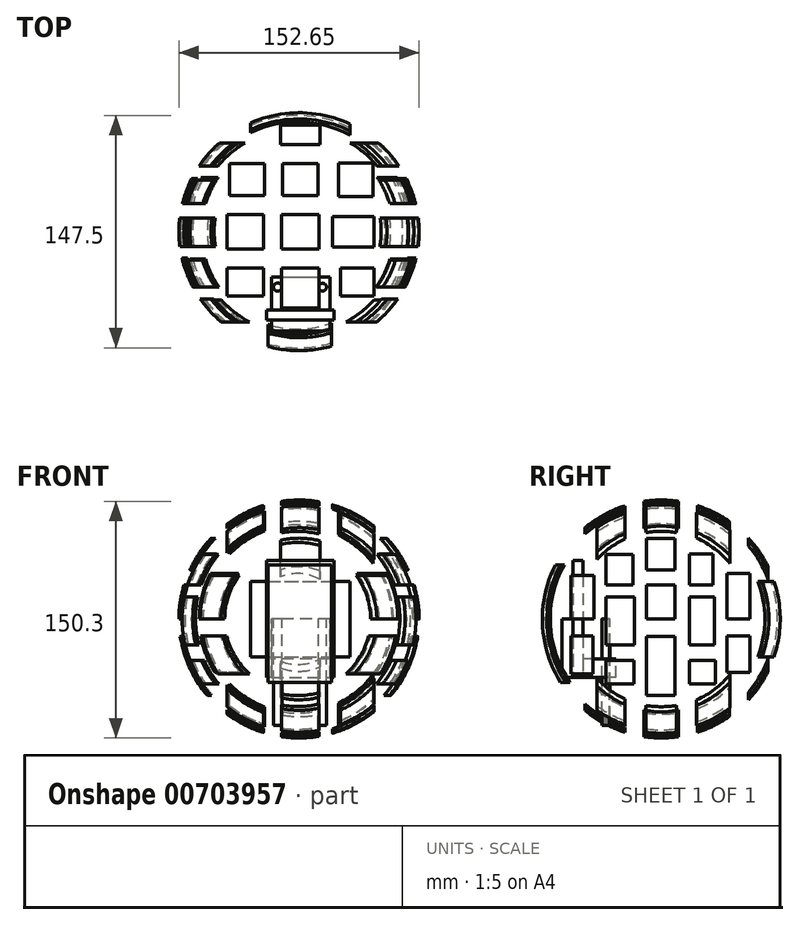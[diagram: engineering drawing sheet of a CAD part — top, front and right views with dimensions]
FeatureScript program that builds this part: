
annotation { "Feature Type Name" : "Feature", "Feature Type Description" : "" }
export const myFeature = defineFeature(function(context is Context, id is Id, definition is map)
    precondition{}
    {
        {
            var Q0;
            Q0=qCreatedBy(makeId("Front.planeOp"),FACE);
            var sketch = newSketch(context, id + "F0", { "sketchPlane" : qUnion([Q0])});
            skArc(sketch, "E0", {"start": v(75.5, 0) * mm, "mid": v(-0.83, 75.54) * mm, "end": v(-77.15, 0) * mm});
            skLineSegment(sketch, "E1", {"start": v(-77.15, 0) * mm, "end": v(75.5, 0) * mm});
            skLineSegment(sketch, "E2", {"start": v(-77.15, 0) * mm, "end": v(-98.73, 0) * mm});
            skLineSegment(sketch, "E3", {"start": v(-98.73, 0) * mm, "end": v(93.51, 0) * mm});
            skSolve(sketch);
        }
        {
            var Q0;
            Q0 = qSketchRegion(id + "F0", true);
            var Q1;
            Q1=sQuery(id+"F0.wireOp",EDGE,"E3");
            revolve(context, id + "F1", {"surfaceOperationType" : NewSurfaceOperationType.NEW, "entities" : qUnion([Q0]), "axis" : qUnion([Q1]), "revolveType" : RevolveType.FULL});
        }
        {
            var Q0;
            Q0=qCreatedBy(makeId("Top.planeOp"),FACE);
            var sketch = newSketch(context, id + "F2", { "sketchPlane" : qUnion([Q0])});
            skLineSegment(sketch, "E4.bottom", {"start": v(11.8, 10.88) * mm, "end": v(-11.8, 10.88) * mm});
            skLineSegment(sketch, "E4.top", {"start": v(11.8, -10.88) * mm, "end": v(-11.8, -10.88) * mm});
            skLineSegment(sketch, "E4.left", {"start": v(11.8, 10.88) * mm, "end": v(11.8, -10.88) * mm});
            skLineSegment(sketch, "E4.right", {"start": v(-11.8, 10.88) * mm, "end": v(-11.8, -10.88) * mm});
            skPoint(sketch, "E4.middle", {"position": v(0, 0) * mm});
            skLineSegment(sketch, "E5.bottom", {"start": v(11.8, -23.05) * mm, "end": v(-11.8, -23.05) * mm});
            skLineSegment(sketch, "E5.top", {"start": v(11.8, -48.4) * mm, "end": v(-11.8, -48.4) * mm});
            skLineSegment(sketch, "E5.left", {"start": v(11.8, -23.05) * mm, "end": v(11.8, -48.4) * mm});
            skLineSegment(sketch, "E5.right", {"start": v(-11.8, -23.05) * mm, "end": v(-11.8, -48.4) * mm});
            skPoint(sketch, "E5.middle", {"position": v(0, -35.72) * mm});
            skPoint(sketch, "E5.middle.positionSnap0", {"position": v(0, -10.88) * mm});
            skPoint(sketch, "E5.centerSnap0", {"position": v(0, -10.88) * mm});
            skLineSegment(sketch, "E6.bottom", {"start": v(11.4, 43.22) * mm, "end": v(-11.4, 43.22) * mm});
            skLineSegment(sketch, "E6.top", {"start": v(11.4, 22.83) * mm, "end": v(-11.4, 22.83) * mm});
            skLineSegment(sketch, "E6.left", {"start": v(11.4, 43.22) * mm, "end": v(11.4, 22.83) * mm});
            skLineSegment(sketch, "E6.right", {"start": v(-11.4, 43.22) * mm, "end": v(-11.4, 22.83) * mm});
            skPoint(sketch, "E6.middle", {"position": v(0, 33.03) * mm});
            skLineSegment(sketch, "E7.bottom", {"start": v(-23.48, 10.88) * mm, "end": v(-46.43, 10.88) * mm});
            skLineSegment(sketch, "E7.top", {"start": v(-23.48, -10.88) * mm, "end": v(-46.43, -10.88) * mm});
            skLineSegment(sketch, "E7.left", {"start": v(-23.48, 10.88) * mm, "end": v(-23.48, -10.88) * mm});
            skLineSegment(sketch, "E7.right", {"start": v(-46.43, 10.88) * mm, "end": v(-46.43, -10.88) * mm});
            skPoint(sketch, "E7.middle", {"position": v(-34.96, 0) * mm});
            skLineSegment(sketch, "E8.bottom", {"start": v(46.66, 9.6) * mm, "end": v(20.3, 9.6) * mm});
            skLineSegment(sketch, "E8.top", {"start": v(46.66, -9.6) * mm, "end": v(20.3, -9.6) * mm});
            skLineSegment(sketch, "E8.left", {"start": v(46.66, 9.6) * mm, "end": v(46.66, -9.6) * mm});
            skLineSegment(sketch, "E8.right", {"start": v(20.3, 9.6) * mm, "end": v(20.3, -9.6) * mm});
            skPoint(sketch, "E8.middle", {"position": v(33.48, 0) * mm});
            skLineSegment(sketch, "E9.bottom", {"start": v(46.24, 43.65) * mm, "end": v(24.12, 43.65) * mm});
            skLineSegment(sketch, "E9.top", {"start": v(46.24, 22.4) * mm, "end": v(24.12, 22.4) * mm});
            skLineSegment(sketch, "E9.left", {"start": v(46.24, 43.65) * mm, "end": v(46.24, 22.4) * mm});
            skLineSegment(sketch, "E9.right", {"start": v(24.12, 43.65) * mm, "end": v(24.12, 22.4) * mm});
            skPoint(sketch, "E9.middle", {"position": v(35.18, 33.03) * mm});
            skLineSegment(sketch, "E10.bottom", {"start": v(-22.6, 43.22) * mm, "end": v(-44.88, 43.22) * mm});
            skLineSegment(sketch, "E10.top", {"start": v(-22.6, 22.83) * mm, "end": v(-44.88, 22.83) * mm});
            skLineSegment(sketch, "E10.left", {"start": v(-22.6, 43.22) * mm, "end": v(-22.6, 22.83) * mm});
            skLineSegment(sketch, "E10.right", {"start": v(-44.88, 43.22) * mm, "end": v(-44.88, 22.83) * mm});
            skPoint(sketch, "E10.middle", {"position": v(-33.74, 33.03) * mm});
            skLineSegment(sketch, "E11.bottom", {"start": v(12.66, 67.86) * mm, "end": v(-12.66, 67.86) * mm});
            skLineSegment(sketch, "E11.top", {"start": v(12.66, 55.43) * mm, "end": v(-12.66, 55.43) * mm});
            skLineSegment(sketch, "E11.left", {"start": v(12.66, 67.86) * mm, "end": v(12.66, 55.43) * mm});
            skLineSegment(sketch, "E11.right", {"start": v(-12.66, 67.86) * mm, "end": v(-12.66, 55.43) * mm});
            skPoint(sketch, "E11.middle", {"position": v(0, 61.65) * mm});
            skLineSegment(sketch, "E12.bottom", {"start": v(46.66, -23.05) * mm, "end": v(25.46, -23.05) * mm});
            skLineSegment(sketch, "E12.top", {"start": v(46.66, -40.9) * mm, "end": v(25.46, -40.9) * mm});
            skLineSegment(sketch, "E12.left", {"start": v(46.66, -23.05) * mm, "end": v(46.66, -40.9) * mm});
            skLineSegment(sketch, "E12.right", {"start": v(25.46, -23.05) * mm, "end": v(25.46, -40.9) * mm});
            skPoint(sketch, "E12.middle", {"position": v(36.06, -31.98) * mm});
            skLineSegment(sketch, "E13.bottom", {"start": v(-23.48, -23.05) * mm, "end": v(-46.43, -23.05) * mm});
            skLineSegment(sketch, "E13.top", {"start": v(-23.48, -40.9) * mm, "end": v(-46.43, -40.9) * mm});
            skLineSegment(sketch, "E13.left", {"start": v(-23.48, -23.05) * mm, "end": v(-23.48, -40.9) * mm});
            skLineSegment(sketch, "E13.right", {"start": v(-46.43, -23.05) * mm, "end": v(-46.43, -40.9) * mm});
            skPoint(sketch, "E13.middle", {"position": v(-34.96, -31.98) * mm});
            skPoint(sketch, "E13.cornerSnap0", {"position": v(-23.48, 0) * mm});
            skSolve(sketch);
        }
        {
            var Q0;
            Q0 = qSketchRegion(id + "F2", true);
            extrude(context, id + "F3", {"entities" : qUnion([Q0]), "operationType" : NewBodyOperationType.REMOVE, "endBound" : BoundingType.SYMMETRIC, "depth" : 301.9 * mm, "offsetDistance" : 25.4 * mm});
        }
        {
            var Q0;
            Q0=qCreatedBy(makeId("Front.planeOp"),FACE);
            var sketch = newSketch(context, id + "F4", { "sketchPlane" : qUnion([Q0])});
            skLineSegment(sketch, "E14", {"start": v(-75.42, 0) * mm, "end": v(72.08, 0) * mm});
            skArc(sketch, "E15", {"start": v(72.08, 0) * mm, "mid": v(-1.67, 73.75) * mm, "end": v(-75.42, 0) * mm});
            skSolve(sketch);
        }
        {
            var Q0;
            Q0 = qSketchRegion(id + "F4", true);
            var Q1;
            Q1=sQuery(id+"F4.wireOp",EDGE,"E14");
            revolve(context, id + "F5", {"operationType" : NewBodyOperationType.REMOVE, "surfaceOperationType" : NewSurfaceOperationType.NEW, "entities" : qUnion([Q0]), "axis" : qUnion([Q1]), "revolveType" : RevolveType.FULL, "oppositeDirection" : true});
        }
        {
            var Q0;
            Q0=qCreatedBy(makeId("Front.planeOp"),FACE);
            var sketch = newSketch(context, id + "F6", { "sketchPlane" : qUnion([Q0])});
            skLineSegment(sketch, "E16.bottom", {"start": v(-20.54, 34.32) * mm, "end": v(19.94, 34.32) * mm});
            skLineSegment(sketch, "E16.top", {"start": v(-20.54, -40.2) * mm, "end": v(19.94, -40.2) * mm});
            skLineSegment(sketch, "E16.left", {"start": v(-20.54, 34.32) * mm, "end": v(-20.54, -40.2) * mm});
            skLineSegment(sketch, "E16.right", {"start": v(19.94, 34.32) * mm, "end": v(19.94, -40.2) * mm});
            skSolve(sketch);
        }
        {
            var Q0;
            Q0 = qSketchRegion(id + "F6", true);
            extrude(context, id + "F7", {"entities" : qUnion([Q0]), "operationType" : NewBodyOperationType.REMOVE, "depth" : 174.95 * mm, "offsetDistance" : 25.4 * mm});
        }
        {
            var Q0;
            Q0=qCreatedBy(makeId("Right.planeOp"),FACE);
            var sketch = newSketch(context, id + "F8", { "sketchPlane" : qUnion([Q0])});
            skLineSegment(sketch, "E17.bottom", {"start": v(-9.27, 51.22) * mm, "end": v(8.56, 51.22) * mm});
            skLineSegment(sketch, "E17.top", {"start": v(-9.27, 31.3) * mm, "end": v(8.56, 31.3) * mm});
            skLineSegment(sketch, "E17.left", {"start": v(-9.27, 51.22) * mm, "end": v(-9.27, 31.3) * mm});
            skLineSegment(sketch, "E17.right", {"start": v(8.56, 51.22) * mm, "end": v(8.56, 31.3) * mm});
            skLineSegment(sketch, "E18.bottom", {"start": v(-18.03, 40.92) * mm, "end": v(-35.01, 40.92) * mm});
            skLineSegment(sketch, "E18.top", {"start": v(-18.03, 21.6) * mm, "end": v(-35.01, 21.6) * mm});
            skLineSegment(sketch, "E18.left", {"start": v(-18.03, 40.92) * mm, "end": v(-18.03, 21.6) * mm});
            skLineSegment(sketch, "E18.right", {"start": v(-35.01, 40.92) * mm, "end": v(-35.01, 21.6) * mm});
            skLineSegment(sketch, "E19.bottom", {"start": v(-57.38, 27.8) * mm, "end": v(-42.72, 27.8) * mm});
            skLineSegment(sketch, "E19.top", {"start": v(-57.38, 0) * mm, "end": v(-42.72, 0) * mm});
            skLineSegment(sketch, "E19.left", {"start": v(-57.38, 27.8) * mm, "end": v(-57.38, 0) * mm});
            skLineSegment(sketch, "E19.right", {"start": v(-42.72, 27.8) * mm, "end": v(-42.72, 0) * mm});
            skLineSegment(sketch, "E20.bottom", {"start": v(-57.38, -10.76) * mm, "end": v(-43.5, -10.76) * mm});
            skLineSegment(sketch, "E20.top", {"start": v(-57.38, -34.79) * mm, "end": v(-43.5, -34.79) * mm});
            skLineSegment(sketch, "E20.left", {"start": v(-57.38, -10.76) * mm, "end": v(-57.38, -34.79) * mm});
            skLineSegment(sketch, "E20.right", {"start": v(-43.5, -10.76) * mm, "end": v(-43.5, -34.79) * mm});
            skPoint(sketch, "E21.firstSnap0", {"position": v(-42.72, 13.9) * mm});
            skLineSegment(sketch, "E21.bottom", {"start": v(-35.01, 13.9) * mm, "end": v(-16.88, 13.9) * mm});
            skLineSegment(sketch, "E21.top", {"start": v(-35.01, -16.55) * mm, "end": v(-16.88, -16.55) * mm});
            skLineSegment(sketch, "E21.left", {"start": v(-35.01, 13.9) * mm, "end": v(-35.01, -16.55) * mm});
            skLineSegment(sketch, "E21.right", {"start": v(-16.88, 13.9) * mm, "end": v(-16.88, -16.55) * mm});
            skLineSegment(sketch, "E22.bottom", {"start": v(-35.01, -26.38) * mm, "end": v(-17.27, -26.38) * mm});
            skLineSegment(sketch, "E22.top", {"start": v(-35.01, -41.29) * mm, "end": v(-17.27, -41.29) * mm});
            skLineSegment(sketch, "E22.left", {"start": v(-35.01, -26.38) * mm, "end": v(-35.01, -41.29) * mm});
            skLineSegment(sketch, "E22.right", {"start": v(-17.27, -26.38) * mm, "end": v(-17.27, -41.29) * mm});
            skLineSegment(sketch, "E23.bottom", {"start": v(-9.27, 21.6) * mm, "end": v(8.56, 21.6) * mm});
            skLineSegment(sketch, "E23.top", {"start": v(-9.27, 0) * mm, "end": v(8.56, 0) * mm});
            skLineSegment(sketch, "E23.left", {"start": v(-9.27, 21.6) * mm, "end": v(-9.27, 0) * mm});
            skLineSegment(sketch, "E23.right", {"start": v(8.56, 21.6) * mm, "end": v(8.56, 0) * mm});
            skLineSegment(sketch, "E24.bottom", {"start": v(-9.27, -11) * mm, "end": v(8.56, -11) * mm});
            skLineSegment(sketch, "E24.top", {"start": v(-9.27, -48.56) * mm, "end": v(8.56, -48.56) * mm});
            skLineSegment(sketch, "E24.left", {"start": v(-9.27, -11) * mm, "end": v(-9.27, -48.56) * mm});
            skLineSegment(sketch, "E24.right", {"start": v(8.56, -11) * mm, "end": v(8.56, -48.56) * mm});
            skPoint(sketch, "E25.firstSnap0", {"position": v(8.56, 41.26) * mm});
            skLineSegment(sketch, "E25.bottom", {"start": v(17.78, 41.26) * mm, "end": v(32.9, 41.26) * mm});
            skLineSegment(sketch, "E25.top", {"start": v(17.78, 21.63) * mm, "end": v(32.9, 21.63) * mm});
            skLineSegment(sketch, "E25.left", {"start": v(17.78, 41.26) * mm, "end": v(17.78, 21.63) * mm});
            skLineSegment(sketch, "E25.right", {"start": v(32.9, 41.26) * mm, "end": v(32.9, 21.63) * mm});
            skLineSegment(sketch, "E26.bottom", {"start": v(17.78, 13.9) * mm, "end": v(33.65, 13.9) * mm});
            skLineSegment(sketch, "E26.top", {"start": v(17.78, -16.55) * mm, "end": v(33.65, -16.55) * mm});
            skLineSegment(sketch, "E26.left", {"start": v(17.78, 13.9) * mm, "end": v(17.78, -16.55) * mm});
            skLineSegment(sketch, "E26.right", {"start": v(33.65, 13.9) * mm, "end": v(33.65, -16.55) * mm});
            skLineSegment(sketch, "E27.bottom", {"start": v(17.78, -26.38) * mm, "end": v(34.44, -26.38) * mm});
            skLineSegment(sketch, "E27.top", {"start": v(17.78, -41.23) * mm, "end": v(34.44, -41.23) * mm});
            skLineSegment(sketch, "E27.left", {"start": v(17.78, -26.38) * mm, "end": v(17.78, -41.23) * mm});
            skLineSegment(sketch, "E27.right", {"start": v(34.44, -26.38) * mm, "end": v(34.44, -41.23) * mm});
            skLineSegment(sketch, "E28.bottom", {"start": v(41.8, 28.96) * mm, "end": v(56.43, 28.96) * mm});
            skLineSegment(sketch, "E28.top", {"start": v(41.8, 0) * mm, "end": v(56.43, 0) * mm});
            skLineSegment(sketch, "E28.left", {"start": v(41.8, 28.96) * mm, "end": v(41.8, 0) * mm});
            skLineSegment(sketch, "E28.right", {"start": v(56.43, 28.96) * mm, "end": v(56.43, 0) * mm});
            skPoint(sketch, "E29.oppositeSnap0", {"position": v(34.44, -33.8) * mm});
            skLineSegment(sketch, "E29.bottom", {"start": v(41.8, -10.76) * mm, "end": v(56.42, -10.76) * mm});
            skLineSegment(sketch, "E29.top", {"start": v(41.8, -33.8) * mm, "end": v(56.42, -33.8) * mm});
            skLineSegment(sketch, "E29.left", {"start": v(41.8, -10.76) * mm, "end": v(41.8, -33.8) * mm});
            skLineSegment(sketch, "E29.right", {"start": v(56.42, -10.76) * mm, "end": v(56.42, -33.8) * mm});
            skSolve(sketch);
        }
        {
            var Q0;
            Q0 = qSketchRegion(id + "F8", true);
            extrude(context, id + "F9", {"entities" : qUnion([Q0]), "operationType" : NewBodyOperationType.REMOVE, "endBound" : BoundingType.SYMMETRIC, "depth" : 251.44 * mm, "offsetDistance" : 25.4 * mm});
        }
        {
            var Q0;
            Q0=qCreatedBy(makeId("Front.planeOp"),FACE);
            var sketch = newSketch(context, id + "F10", { "sketchPlane" : qUnion([Q0])});
            skLineSegment(sketch, "E30.bottom", {"start": v(-31.6, 24) * mm, "end": v(31.6, 24) * mm});
            skLineSegment(sketch, "E30.top", {"start": v(-31.6, -24) * mm, "end": v(31.6, -24) * mm});
            skLineSegment(sketch, "E30.left", {"start": v(-31.6, 24) * mm, "end": v(-31.6, -24) * mm});
            skLineSegment(sketch, "E30.right", {"start": v(31.6, 24) * mm, "end": v(31.6, -24) * mm});
            skPoint(sketch, "E30.middle", {"position": v(0, 0) * mm});
            skSolve(sketch);
        }
        {
            var Q0;
            Q0 = qSketchRegion(id + "F10", true);
            extrude(context, id + "F11", {"entities" : qUnion([Q0]), "operationType" : NewBodyOperationType.REMOVE, "oppositeDirection" : true, "depth" : 141.65 * mm, "offsetDistance" : 25.4 * mm});
        }
        {
            var Q0;
            Q0=qCreatedBy(makeId("Top.planeOp"),FACE);
            var sketch = newSketch(context, id + "F12", { "sketchPlane" : qUnion([Q0])});
            skLineSegment(sketch, "E31.bottom", {"start": v(21.44, -49.8) * mm, "end": v(-21.44, -49.8) * mm});
            skLineSegment(sketch, "E31.top", {"start": v(21.44, -56) * mm, "end": v(-21.44, -56) * mm});
            skLineSegment(sketch, "E31.left", {"start": v(21.44, -49.8) * mm, "end": v(21.44, -56) * mm});
            skLineSegment(sketch, "E31.right", {"start": v(-21.44, -49.8) * mm, "end": v(-21.44, -56) * mm});
            skPoint(sketch, "E31.middle", {"position": v(0, -52.9) * mm});
            skSolve(sketch);
        }
        {
            var Q0;
            Q0 = qSketchRegion(id + "F12", true);
            extrude(context, id + "F13", {"entities" : qUnion([Q0]), "endBound" : BoundingType.SYMMETRIC, "depth" : 74.4 * mm, "offsetDistance" : 25.4 * mm});
        }
        {
            var Q0;
            Q0=qCreatedBy(makeId("Top.planeOp"),FACE);
            var sketch = newSketch(context, id + "F14", { "sketchPlane" : qUnion([Q0])});
            skLineSegment(sketch, "E32.bottom", {"start": v(-18.28, -28.73) * mm, "end": v(18.8, -28.73) * mm});
            skLineSegment(sketch, "E32.top", {"start": v(-18.28, -62.98) * mm, "end": v(18.8, -62.98) * mm});
            skLineSegment(sketch, "E32.left", {"start": v(-18.28, -28.73) * mm, "end": v(-18.28, -62.98) * mm});
            skLineSegment(sketch, "E32.right", {"start": v(18.8, -28.73) * mm, "end": v(18.8, -62.98) * mm});
            skSolve(sketch);
        }
        {
            var Q0;
            Q0=makeQuery(id+"F14.imprint","IMPRINT",FACE,{"disambiguationData":[TD([[makeQuery(id+"F14.imprint","IMPRINT",EDGE,{"derivedFrom":sQuery(id+"F14.wireOp",EDGE,"E32.bottom")}),-1.0]])]});
            var Q1;
            Q1=sQuery(id+"F14.wireOp",EDGE,"E32.bottom");
            extrude(context, id + "F15", {"entities" : qUnion([Q0]), "operationType" : NewBodyOperationType.ADD, "surfaceEntities" : qUnion([Q1]), "oppositeDirection" : true, "depth" : 37.2 * mm, "offsetDistance" : 25.4 * mm});
        }
        {
            var Q0;
            {var subQ0=sQuery(id+"F14.wireOp",EDGE,"E32.bottom");var subQ1=sQuery(id+"F14.wireOp",EDGE,"E32.right");var subQ2=sQuery(id+"F14.wireOp",EDGE,"E32.left");Q0=makeQuery(id+"F15.boolean.opBoolean","SPLIT",FACE,{"disambiguationData":[TD([makeQuery(id+"F13.opExtrude","SWEPT_FACE",FACE,{"disambiguationData":[OSD([sQuery(id+"F12.wireOp",EDGE,"E31.bottom")])]})])],"derivedFrom":makeQuery(id+"F15.opExtrude","CAP_FACE",FACE,{"disambiguationData":[OSD([subQ0,sQuery(id+"F14.wireOp",EDGE,"E32.top"),subQ2,subQ1])],"isStart":true})});}
            extrude(context, id + "F16", {"entities" : qUnion([Q0]), "operationType" : NewBodyOperationType.REMOVE, "oppositeDirection" : true, "depth" : 25.4 * mm, "offsetDistance" : 25.4 * mm});
        }
        {
            var Q0;
            Q0=qCreatedBy(makeId("Top.planeOp"),FACE);
            var sketch = newSketch(context, id + "F17", { "sketchPlane" : qUnion([Q0])});
            skCircle(sketch, "E33", {"center": v(-14.35, -35.23) * mm, "radius": 2.6 * mm});
            skCircle(sketch, "E34", {"center": v(14.17, -35.23) * mm, "radius": 2.46 * mm});
            skSolve(sketch);
        }
        {
            var Q0;
            Q0 = qSketchRegion(id + "F17", true);
            extrude(context, id + "F18", {"entities" : qUnion([Q0]), "oppositeDirection" : true, "depth" : 67.5 * mm, "offsetDistance" : 25.4 * mm});
        }
    });
